# Revit family: Pump_Commercial-Effluent-Zoeller-151
name_source: partatom
category: Mechanical Equipment
revit_build: Autodesk Revit 2014 (Build: 20130308_1515(x64)
units: mm (PartAtom-declared; Revit-internal decimal feet)

## types (2) — shared parameters
Assembly Code = D2010900
Cord Length = 240"
Cord Type = UL listed.
Default Elevation = 0"
Description = Commercial Sewage Pumps
Discharge Diameter = 1 1/2" NPT
Discharge Height = 4 15/16"
Discharge Radius = 3/4"
Height = 11 11/16"
Hertz = 60
Impeller Type = Non-clogging thermoplastic vortex design
Installation Type = Floor Mounted
Insulation = Class B
Lead Wires Insulation = Class B
Length = 10 3/32"
Manufacturer = Zoeller
Material = Cast Iron-Zoeller-Powder Coated Epoxy
Max Flow @ 5' = 50 GPM
Max. Flow at Min. Head = 50 GPM @ 5'
Max. Water Temp. = 130 °F
Maximum Head = 360"
Minimum Head = 60"
Model = 151
Motor = 1/3 HP
Motor Design Letter = NEMA B
Motor Thermal Shutoff = Auto Reset Thermal Overload.
Motor Type = Submersible
O-Rings and Cover Gasket = Neoprene
Operation = Automatic or nonautomatic
Phase = 1
Price = Prices may vary. Please consult Manufacturer Representative for most up-to-date price list.
Product Page URL = http://www.zoellerpumps.com
Service Factor = 1.15
Shaft Seal = Carbon/Ceramic
Shipping Weight = 93-96 lbs
Type = Permanent Split Capacitor
URL = http://www.zoellerpumps.com
Warranty Information = 36 Months (Limited)
Waste Connection = Yes
Width = 7 3/4"

## per-type parameters (varying)
| type | Amps | Apparent Load | Voltage |
| 151 - 115V 1Ph | 6 A | 690 VA | 115 V |
| 151 - 230V 1Ph | 3 A | 736 VA | 230 V |

## geometry (parser evidence)
native form markers: Sweep x2
no freeform markers — native parametric forms only
